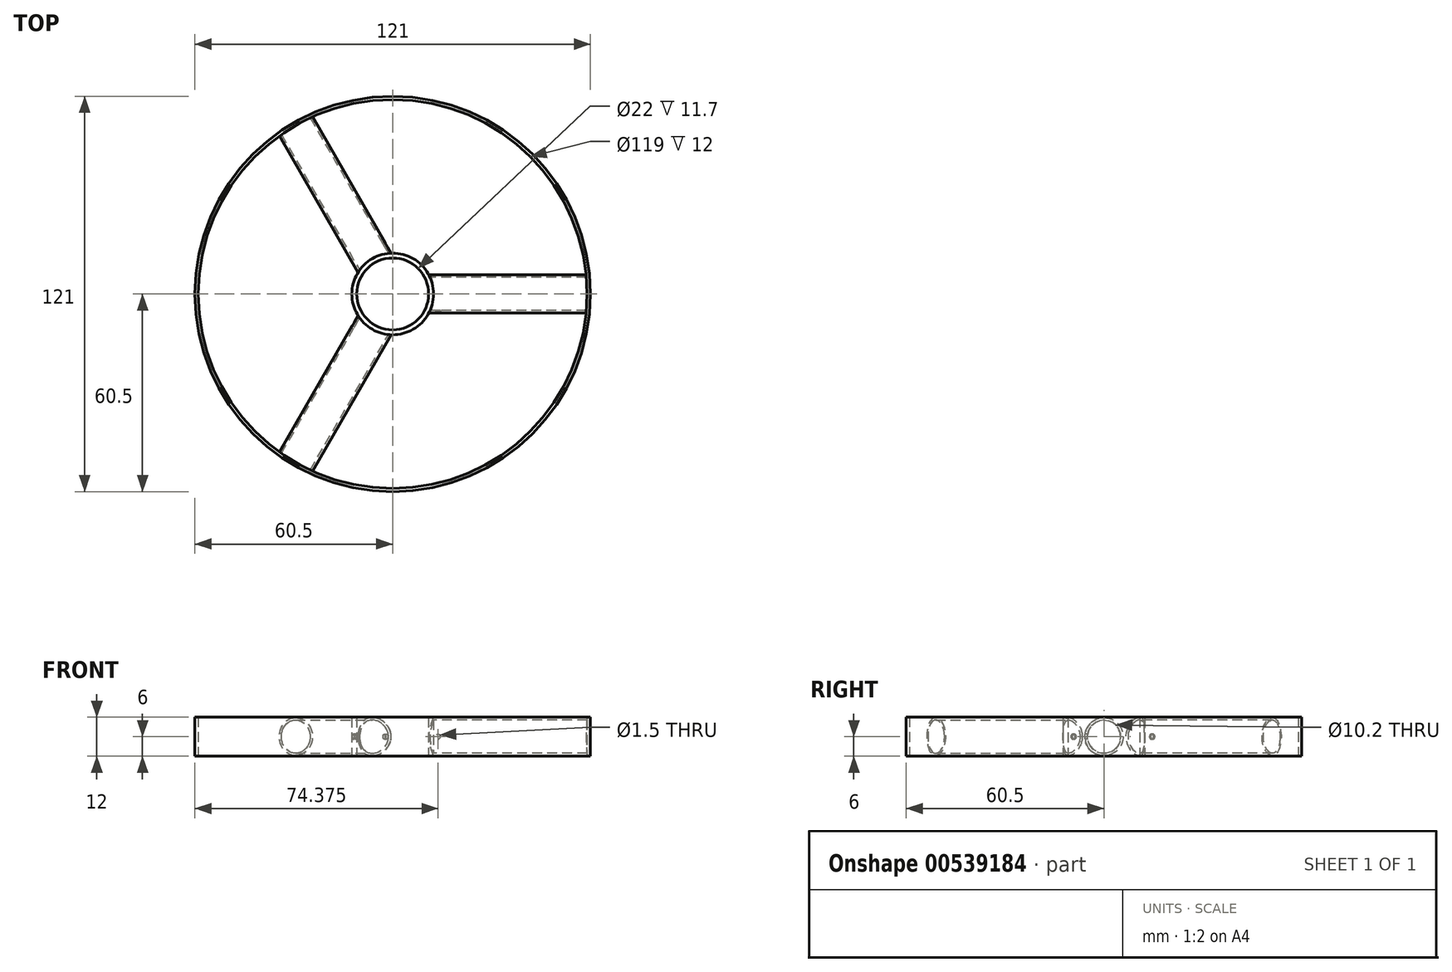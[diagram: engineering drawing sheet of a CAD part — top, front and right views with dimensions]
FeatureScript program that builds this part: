
annotation { "Feature Type Name" : "Feature", "Feature Type Description" : "" }
export const myFeature = defineFeature(function(context is Context, id is Id, definition is map)
    precondition{}
    {
        {
            var Q0;
            Q0=qCreatedBy(makeId("Top.planeOp"),FACE);
            var sketch = newSketch(context, id + "F0", { "sketchPlane" : qUnion([Q0])});
            skCircle(sketch, "E0", {"center": v(0, 0) * mm, "radius": 11 * mm});
            skCircle(sketch, "E1", {"center": v(0, 0) * mm, "radius": 12.5 * mm});
            skLineSegment(sketch, "E2.0", {"start": v(-29.75, 51.53) * mm, "end": v(29.75, 51.53) * mm, "construction": true});
            skLineSegment(sketch, "E2.1", {"start": v(29.75, 51.53) * mm, "end": v(59.5, 0) * mm, "construction": true});
            skLineSegment(sketch, "E2.2", {"start": v(59.5, 0) * mm, "end": v(29.75, -51.53) * mm, "construction": true});
            skLineSegment(sketch, "E2.3", {"start": v(29.75, -51.53) * mm, "end": v(-29.75, -51.53) * mm, "construction": true});
            skLineSegment(sketch, "E2.4", {"start": v(-29.75, -51.53) * mm, "end": v(-59.5, 0) * mm, "construction": true});
            skLineSegment(sketch, "E2.5", {"start": v(-59.5, 0) * mm, "end": v(-29.75, 51.53) * mm, "construction": true});
            skPoint(sketch, "E2.0.midPoint", {"position": v(0, 51.53) * mm});
            skLineSegment(sketch, "E3", {"start": v(-29.75, 51.53) * mm, "end": v(-6.25, 10.83) * mm});
            skLineSegment(sketch, "E4", {"start": v(12.5, 0) * mm, "end": v(59.5, 0) * mm});
            skLineSegment(sketch, "E5", {"start": v(-6.25, -10.83) * mm, "end": v(-29.75, -51.53) * mm});
            skPoint(sketch, "E6", {"position": v(-6.94, 12.02) * mm});
            skPoint(sketch, "E7", {"position": v(-29.06, 50.34) * mm});
            skPoint(sketch, "E8", {"position": v(58.13, 0) * mm});
            skPoint(sketch, "E9", {"position": v(13.88, 0) * mm});
            skPoint(sketch, "E10", {"position": v(-29.06, -50.34) * mm});
            skPoint(sketch, "E11", {"position": v(-6.94, -12.02) * mm});
            skLineSegment(sketch, "E12", {"start": v(-6.25, 10.83) * mm, "end": v(-5.5, 9.53) * mm});
            skCircle(sketch, "E13", {"center": v(0, 0) * mm, "radius": 59.5 * mm});
            skCircle(sketch, "E14", {"center": v(0, 0) * mm, "radius": 60.5 * mm});
            skSolve(sketch);
        }
        {
            var Q0;
            Q0=makeQuery(id+"F0.imprint","IMPRINT",FACE,{"disambiguationData":[TD([[makeQuery(id+"F0.imprint","IMPRINT",EDGE,{"derivedFrom":sQuery(id+"F0.wireOp",EDGE,"E0")}),-1.0]])]});
            extrude(context, id + "F1", {"entities" : qUnion([Q0]), "endBound" : BoundingType.SYMMETRIC, "depth" : 11.7 * mm, "offsetDistance" : 25 * mm});
        }
        {
            var Q0;
            Q0=sQuery(id+"F0.wireOp",EDGE,"E3");
            var Q1;
            Q1=sQuery(id+"F0.wireOp",VERTEX,"E3.end");
            cPlane(context, id + "F2", {"entities" : qUnion([Q0, Q1]), "cplaneType" : CPlaneType.CURVE_POINT, "offset" : 25 * mm, "width" : 150 * mm, "height" : 150 * mm});
        }
        {
            var Q0;
            Q0=qCreatedBy(id+"F2.planeOp",FACE);
            var sketch = newSketch(context, id + "F3", { "sketchPlane" : qUnion([Q0])});
            skCircle(sketch, "E15", {"center": v(0, 0) * mm, "radius": 5.1 * mm});
            skCircle(sketch, "E16", {"center": v(0, 0) * mm, "radius": 5.85 * mm});
            skSolve(sketch);
        }
        {
            var Q0;
            Q0=makeQuery(id+"F3.imprint","IMPRINT",FACE,{"disambiguationData":[TD([[makeQuery(id+"F3.imprint","IMPRINT",EDGE,{"derivedFrom":sQuery(id+"F3.wireOp",EDGE,"E15")}),-1.0]])]});
            var Q1;
            Q1=sQuery(id+"F3.wireOp",EDGE,"E15");
            var Q2;
            Q2=sQuery(id+"F3.wireOp",EDGE,"E16");
            extrude(context, id + "F4", {"entities" : qUnion([Q0]), "surfaceEntities" : qUnion([Q1, Q2]), "oppositeDirection" : true, "depth" : 47 * mm, "offsetDistance" : 25 * mm, "hasSecondDirection" : true, "secondDirectionOppositeDirection" : false, "secondDirectionDepth" : 1.5 * mm});
        }
        {
            var Q0;
            Q0=sQuery(id+"F0.wireOp",EDGE,"E5");
            var Q1;
            Q1=sQuery(id+"F0.wireOp",VERTEX,"E5.start");
            cPlane(context, id + "F5", {"entities" : qUnion([Q0, Q1]), "cplaneType" : CPlaneType.CURVE_POINT, "offset" : 25 * mm, "width" : 150 * mm, "height" : 150 * mm});
        }
        {
            var Q0;
            Q0=qCreatedBy(id+"F5.planeOp",FACE);
            var sketch = newSketch(context, id + "F6", { "sketchPlane" : qUnion([Q0])});
            skCircle(sketch, "E17", {"center": v(0, 0) * mm, "radius": 5.1 * mm});
            skCircle(sketch, "E18", {"center": v(0, 0) * mm, "radius": 5.85 * mm});
            skSolve(sketch);
        }
        {
            var Q0;
            Q0=makeQuery(id+"F6.imprint","IMPRINT",FACE,{"disambiguationData":[TD([[makeQuery(id+"F6.imprint","IMPRINT",EDGE,{"derivedFrom":sQuery(id+"F6.wireOp",EDGE,"E17")}),-1.0]])]});
            extrude(context, id + "F7", {"entities" : qUnion([Q0]), "operationType" : NewBodyOperationType.ADD, "depth" : 47 * mm, "offsetDistance" : 25 * mm, "hasSecondDirection" : true, "secondDirectionOppositeDirection" : true, "secondDirectionDepth" : 1.4 * mm});
        }
        {
            var Q0;
            Q0=sQuery(id+"F0.wireOp",EDGE,"E4");
            var Q1;
            Q1=sQuery(id+"F0.wireOp",VERTEX,"E4.start");
            cPlane(context, id + "F8", {"entities" : qUnion([Q0, Q1]), "cplaneType" : CPlaneType.CURVE_POINT, "offset" : 25 * mm, "width" : 150 * mm, "height" : 150 * mm});
        }
        {
            var Q0;
            Q0=qCreatedBy(id+"F8.planeOp",FACE);
            var sketch = newSketch(context, id + "F9", { "sketchPlane" : qUnion([Q0])});
            skCircle(sketch, "E19", {"center": v(0, 0) * mm, "radius": 5.1 * mm});
            skCircle(sketch, "E20", {"center": v(0, 0) * mm, "radius": 5.85 * mm});
            skSolve(sketch);
        }
        {
            var Q0;
            Q0=makeQuery(id+"F9.imprint","IMPRINT",FACE,{"disambiguationData":[TD([[makeQuery(id+"F9.imprint","IMPRINT",EDGE,{"derivedFrom":sQuery(id+"F9.wireOp",EDGE,"E19")}),-1.0]])]});
            extrude(context, id + "F10", {"entities" : qUnion([Q0]), "operationType" : NewBodyOperationType.ADD, "depth" : 47 * mm, "offsetDistance" : 25 * mm, "hasSecondDirection" : true, "secondDirectionOppositeDirection" : true, "secondDirectionDepth" : 1.5 * mm});
        }
        {
            var Q0;
            Q0=sQuery(id+"F0.wireOp",EDGE,"E5");
            cPlane(context, id + "F11", {"entities" : qUnion([Q0]), "cplaneType" : CPlaneType.LINE_ANGLE, "offset" : 25 * mm, "angle" : 90 * degree, "oppositeDirection" : true, "width" : 150 * mm, "height" : 150 * mm});
        }
        {
            var Q0;
            Q0=qCreatedBy(id+"F11.planeOp",FACE);
            cPlane(context, id + "F12", {"entities" : qUnion([Q0]), "cplaneType" : CPlaneType.OFFSET, "offset" : 5.85 * mm, "width" : 150 * mm, "height" : 150 * mm});
        }
        {
            var Q0;
            Q0=qCreatedBy(id+"F12.planeOp",FACE);
            var sketch = newSketch(context, id + "F13", { "sketchPlane" : qUnion([Q0])});
            skCircle(sketch, "E21", {"center": v(13.87, 0) * mm, "radius": 0.75 * mm});
            skSolve(sketch);
        }
        {
            var Q0;
            Q0=makeQuery(id+"F13.imprint","IMPRINT",FACE,{"disambiguationData":[TD([[makeQuery(id+"F13.imprint","IMPRINT",EDGE,{"derivedFrom":sQuery(id+"F13.wireOp",EDGE,"E21")}),1.0]])]});
            extrude(context, id + "F14", {"entities" : qUnion([Q0]), "operationType" : NewBodyOperationType.REMOVE, "oppositeDirection" : true, "depth" : 2 * mm, "offsetDistance" : 25 * mm});
        }
        {
            var Q0;
            Q0=sQuery(id+"F0.wireOp",EDGE,"E3");
            cPlane(context, id + "F15", {"entities" : qUnion([Q0]), "cplaneType" : CPlaneType.LINE_ANGLE, "offset" : 25 * mm, "angle" : 90 * degree, "width" : 150 * mm, "height" : 150 * mm});
        }
        {
            var Q0;
            Q0=qCreatedBy(id+"F15.planeOp",FACE);
            cPlane(context, id + "F16", {"entities" : qUnion([Q0]), "cplaneType" : CPlaneType.OFFSET, "offset" : 5.85 * mm, "width" : 150 * mm, "height" : 150 * mm});
        }
        {
            var Q0;
            Q0=qCreatedBy(id+"F16.planeOp",FACE);
            var sketch = newSketch(context, id + "F17", { "sketchPlane" : qUnion([Q0])});
            skCircle(sketch, "E22", {"center": v(13.88, 0) * mm, "radius": 0.75 * mm});
            skSolve(sketch);
        }
        {
            var Q0;
            Q0=makeQuery(id+"F17.imprint","IMPRINT",FACE,{"disambiguationData":[TD([[makeQuery(id+"F17.imprint","IMPRINT",EDGE,{"derivedFrom":sQuery(id+"F17.wireOp",EDGE,"E22")}),1.0]])]});
            extrude(context, id + "F18", {"entities" : qUnion([Q0]), "operationType" : NewBodyOperationType.REMOVE, "oppositeDirection" : true, "depth" : 1.5 * mm, "offsetDistance" : 25 * mm});
        }
        {
            var Q0;
            Q0=sQuery(id+"F0.wireOp",EDGE,"E4");
            cPlane(context, id + "F19", {"entities" : qUnion([Q0]), "cplaneType" : CPlaneType.LINE_ANGLE, "offset" : 25 * mm, "angle" : 0 * degree, "width" : 150 * mm, "height" : 150 * mm});
        }
        {
            var Q0;
            Q0=qCreatedBy(id+"F19.planeOp",FACE);
            cPlane(context, id + "F20", {"entities" : qUnion([Q0]), "cplaneType" : CPlaneType.OFFSET, "offset" : 5.85 * mm, "oppositeDirection" : true, "width" : 150 * mm, "height" : 150 * mm});
        }
        {
            var Q0;
            Q0=qCreatedBy(id+"F20.planeOp",FACE);
            var sketch = newSketch(context, id + "F21", { "sketchPlane" : qUnion([Q0])});
            skCircle(sketch, "E23", {"center": v(-13.88, 0) * mm, "radius": 0.75 * mm});
            skSolve(sketch);
        }
        {
            var Q0;
            Q0=makeQuery(id+"F21.imprint","IMPRINT",FACE,{"disambiguationData":[TD([[makeQuery(id+"F21.imprint","IMPRINT",EDGE,{"derivedFrom":sQuery(id+"F21.wireOp",EDGE,"E23")}),1.0]])]});
            extrude(context, id + "F22", {"entities" : qUnion([Q0]), "operationType" : NewBodyOperationType.REMOVE, "depth" : 1.5 * mm, "offsetDistance" : 25 * mm});
        }
        {
            var Q0;
            Q0=makeQuery(id+"F0.imprint","IMPRINT",FACE,{"disambiguationData":[TD([[makeQuery(id+"F0.imprint","IMPRINT",EDGE,{"derivedFrom":sQuery(id+"F0.wireOp",EDGE,"E14")}),1.0]])]});
            var Q1;
            Q1=sQuery(id+"F0.wireOp",EDGE,"E14");
            var Q2;
            Q2=sQuery(id+"F0.wireOp",EDGE,"E13");
            extrude(context, id + "F23", {"entities" : qUnion([Q0]), "operationType" : NewBodyOperationType.ADD, "surfaceEntities" : qUnion([Q1, Q2]), "endBound" : BoundingType.SYMMETRIC, "depth" : 12 * mm, "offsetDistance" : 25 * mm});
        }
    });
